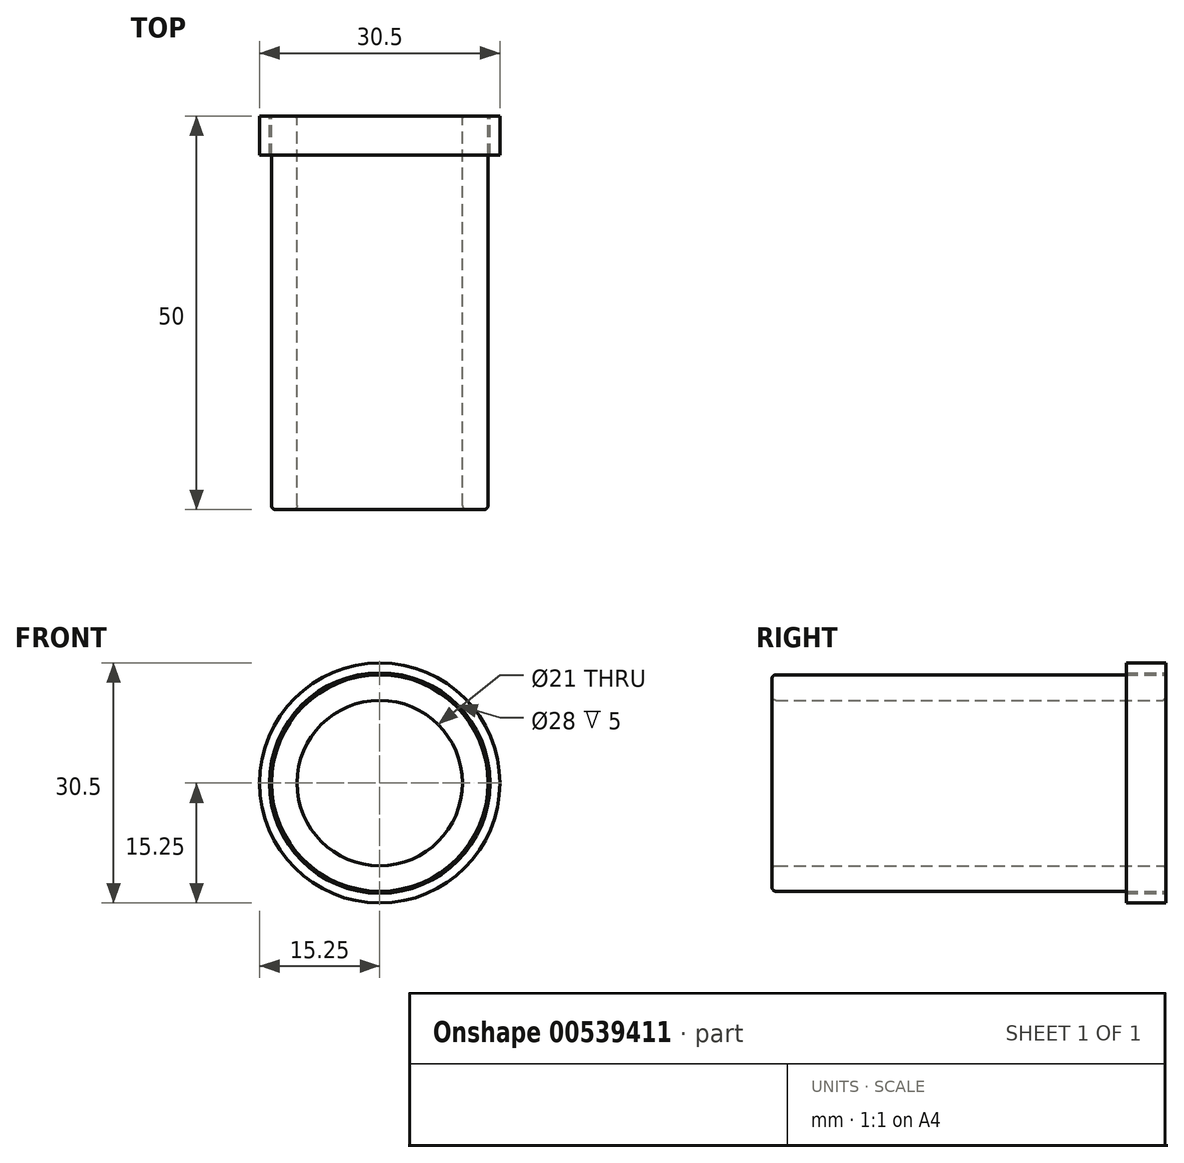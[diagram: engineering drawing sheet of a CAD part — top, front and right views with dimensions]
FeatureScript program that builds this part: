
annotation { "Feature Type Name" : "Feature", "Feature Type Description" : "" }
export const myFeature = defineFeature(function(context is Context, id is Id, definition is map)
    precondition{}
    {
        {
            var Q0;
            Q0=qCreatedBy(makeId("Front.planeOp"),FACE);
            var sketch = newSketch(context, id + "F0", { "sketchPlane" : qUnion([Q0])});
            skCircle(sketch, "E0", {"center": v(0, 0) * mm, "radius": 15.25 * mm});
            skCircle(sketch, "E1", {"center": v(0, 0) * mm, "radius": 14 * mm});
            skCircle(sketch, "E2", {"center": v(0, 0) * mm, "radius": 13.75 * mm});
            skCircle(sketch, "E3", {"center": v(0, 0) * mm, "radius": 10.5 * mm});
            skSolve(sketch);
        }
        {
            var Q0;
            Q0=makeQuery(id+"F0.imprint","IMPRINT",FACE,{"disambiguationData":[TD([[makeQuery(id+"F0.imprint","IMPRINT",EDGE,{"derivedFrom":sQuery(id+"F0.wireOp",EDGE,"E0")}),1.0]])]});
            var Q1;
            Q1=sQuery(id+"F0.wireOp",EDGE,"E0");
            var Q2;
            Q2=sQuery(id+"F0.wireOp",EDGE,"E2");
            extrude(context, id + "F1", {"entities" : qUnion([Q0]), "surfaceEntities" : qUnion([Q1, Q2]), "depth" : 5 * mm, "offsetDistance" : 25 * mm});
        }
        {
            var Q0;
            Q0=sQuery(id+"F0.wireOp",EDGE,"E1");
            var Q1;
            Q1=sQuery(id+"F0.wireOp",EDGE,"E2");
            extrude(context, id + "F2", {"bodyType" : ToolBodyType.SURFACE, "surfaceEntities" : qUnion([Q0, Q1]), "depth" : 25 * mm, "offsetDistance" : 25 * mm});
        }
        {
            var Q0;
            Q0=makeQuery(id+"F0.imprint","IMPRINT",FACE,{"disambiguationData":[TD([[makeQuery(id+"F0.imprint","IMPRINT",EDGE,{"derivedFrom":sQuery(id+"F0.wireOp",EDGE,"E2")}),1.0]])]});
            extrude(context, id + "F3", {"entities" : qUnion([Q0]), "depth" : 50 * mm, "offsetDistance" : 25 * mm});
        }
        {
            var Q0;
            Q0=makeQuery(id+"F3.opExtrude","CAP_EDGE",EDGE,{"disambiguationData":[OSD([sQuery(id+"F0.wireOp",EDGE,"E2")])],"isStart":false});
            var Q1;
            Q1=makeQuery(id+"F3.opExtrude","CAP_EDGE",EDGE,{"disambiguationData":[OSD([sQuery(id+"F0.wireOp",EDGE,"E3")])],"isStart":false});
            fillet(context, id + "F4", {"entities" : qUnion([Q0, Q1]), "radius" : 0.5 * mm, "tangentPropagation" : true, "allowEdgeOverflow" : false});
        }
        {
            var Q0;
            Q0=makeQuery(id+"F3.opExtrude","CAP_EDGE",EDGE,{"disambiguationData":[OSD([sQuery(id+"F0.wireOp",EDGE,"E3")])],"isStart":true});
            fillet(context, id + "F5", {"entities" : qUnion([Q0]), "radius" : 0.5 * mm, "tangentPropagation" : true, "allowEdgeOverflow" : false});
        }
    });
